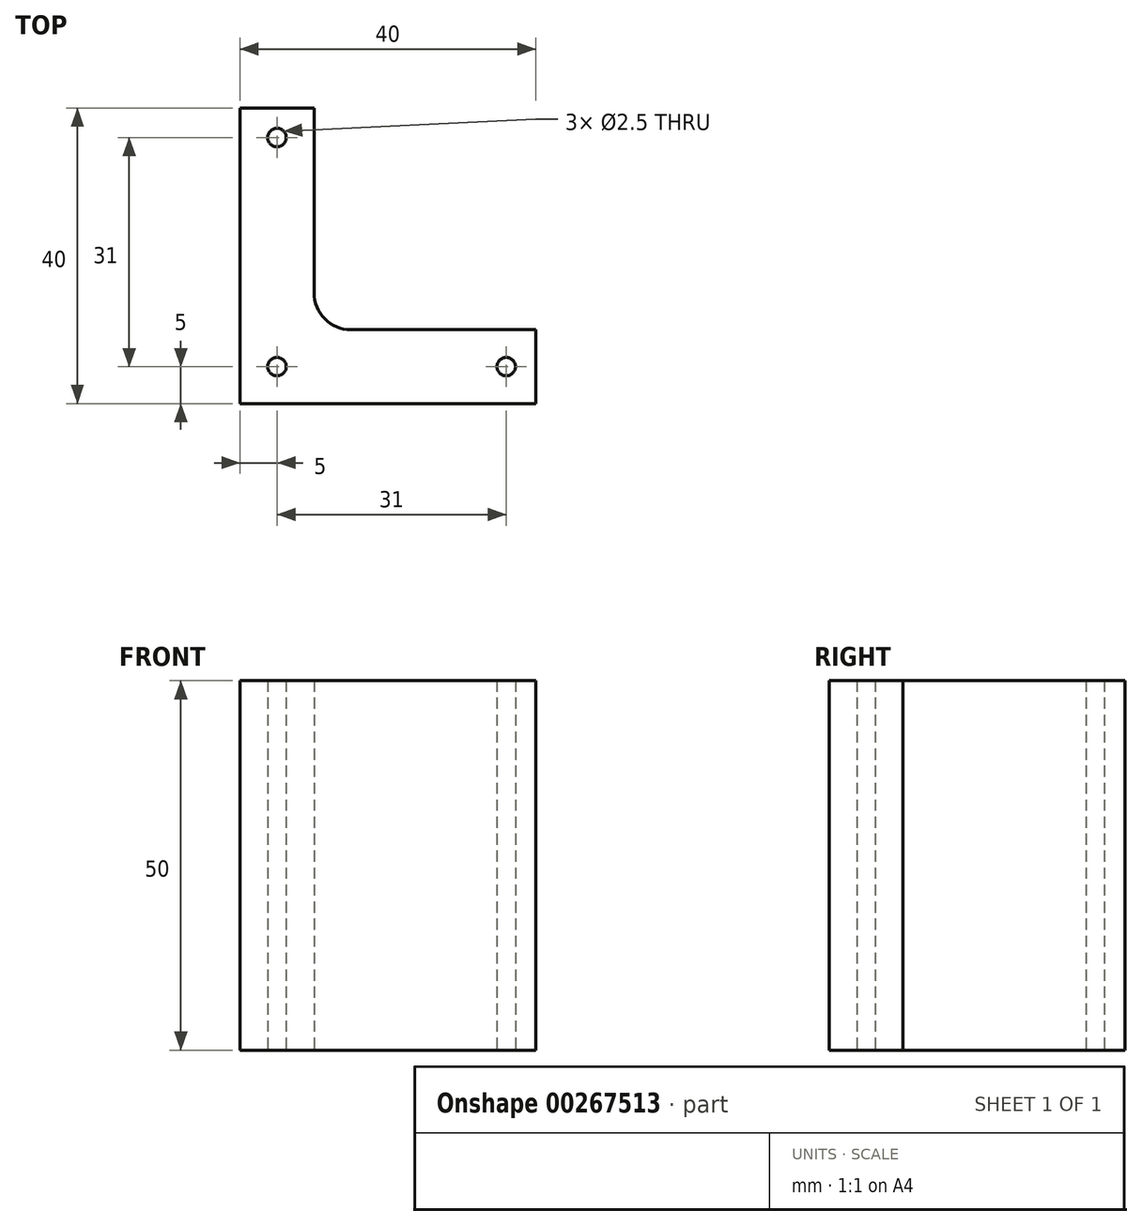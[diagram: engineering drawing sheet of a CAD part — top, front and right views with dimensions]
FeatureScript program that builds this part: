
annotation { "Feature Type Name" : "Feature", "Feature Type Description" : "" }
export const myFeature = defineFeature(function(context is Context, id is Id, definition is map)
    precondition{}
    {
        {
            var Q0;
            Q0=qCreatedBy(makeId("Top.planeOp"),FACE);
            var sketch = newSketch(context, id + "F0", { "sketchPlane" : qUnion([Q0])});
            skLineSegment(sketch, "E0", {"start": v(0, 40) * mm, "end": v(0, 0) * mm});
            skLineSegment(sketch, "E1", {"start": v(0, 0) * mm, "end": v(40, 0) * mm});
            skLineSegment(sketch, "E2", {"start": v(40, 0) * mm, "end": v(40, 10) * mm});
            skLineSegment(sketch, "E3", {"start": v(40, 10) * mm, "end": v(10, 10) * mm});
            skLineSegment(sketch, "E4", {"start": v(10, 10) * mm, "end": v(10, 40) * mm});
            skLineSegment(sketch, "E5", {"start": v(10, 40) * mm, "end": v(0, 40) * mm});
            skCircle(sketch, "E6", {"center": v(5, 36) * mm, "radius": 1.25 * mm});
            skCircle(sketch, "E7", {"center": v(5, 5) * mm, "radius": 1.25 * mm});
            skCircle(sketch, "E8", {"center": v(36, 5) * mm, "radius": 1.25 * mm});
            skPoint(sketch, "E8.centerSnap0", {"position": v(40, 5) * mm});
            skLineSegment(sketch, "E9", {"start": v(5, 36) * mm, "end": v(5, 40) * mm, "construction": true});
            skLineSegment(sketch, "E10", {"start": v(5, 36) * mm, "end": v(5, 5) * mm, "construction": true});
            skLineSegment(sketch, "E11", {"start": v(5, 5) * mm, "end": v(36, 5) * mm, "construction": true});
            skLineSegment(sketch, "E12", {"start": v(36, 5) * mm, "end": v(40, 5) * mm, "construction": true});
            skSolve(sketch);
        }
        {
            var Q0;
            Q0 = qSketchRegion(id + "F0", true);
            extrude(context, id + "F1", {"entities" : qUnion([Q0]), "depth" : 50 * mm});
        }
        {
            var Q0;
            Q0=makeQuery(id+"F1.opExtrude","SWEPT_EDGE",EDGE,{"disambiguationData":[OSD([sQuery(id+"F0.wireOp",EDGE,"E3"),sQuery(id+"F0.wireOp",EDGE,"E4")])]});
            fillet(context, id + "F2", {"entities" : qUnion([Q0]), "radius" : 5 * mm, "tangentPropagation" : true, "allowEdgeOverflow" : false});
        }
    });
